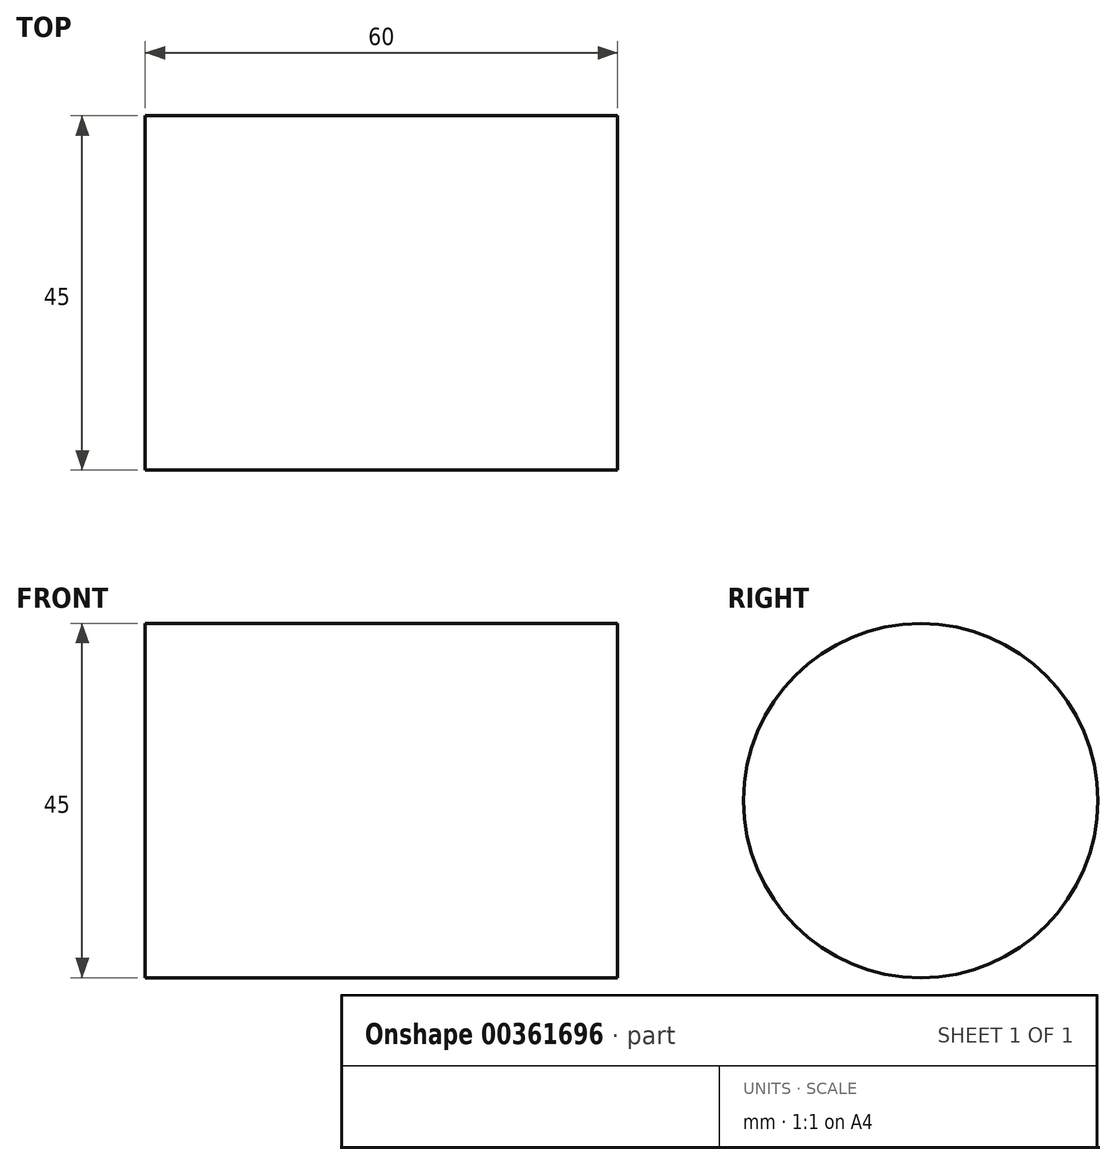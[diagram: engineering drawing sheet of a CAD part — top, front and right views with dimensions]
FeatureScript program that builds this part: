
annotation { "Feature Type Name" : "Feature", "Feature Type Description" : "" }
export const myFeature = defineFeature(function(context is Context, id is Id, definition is map)
    precondition{}
    {
        {
            var Q0;
            Q0=qCreatedBy(makeId("Front.planeOp"),FACE);
            var sketch = newSketch(context, id + "F0", { "sketchPlane" : qUnion([Q0])});
            skLineSegment(sketch, "E0", {"start": v(0, 0) * mm, "end": v(127.89, 0) * mm, "construction": true});
            skLineSegment(sketch, "E1.bottom", {"start": v(0, 22.5) * mm, "end": v(60, 22.5) * mm});
            skLineSegment(sketch, "E1.top", {"start": v(0, 0) * mm, "end": v(60, 0) * mm});
            skLineSegment(sketch, "E1.left", {"start": v(0, 22.5) * mm, "end": v(0, 0) * mm});
            skLineSegment(sketch, "E1.right", {"start": v(60, 22.5) * mm, "end": v(60, 0) * mm});
            skSolve(sketch);
        }
        {
            var Q0;
            Q0=makeQuery(id+"F0.imprint","IMPRINT",FACE,{"disambiguationData":[TD([[makeQuery(id+"F0.imprint","IMPRINT",EDGE,{"derivedFrom":sQuery(id+"F0.wireOp",EDGE,"E1.bottom")}),-1.0]])]});
            var Q1;
            Q1=sQuery(id+"F0.wireOp",EDGE,"E0");
            revolve(context, id + "F1", {"entities" : qUnion([Q0]), "axis" : qUnion([Q1]), "revolveType" : RevolveType.FULL});
        }
    });
